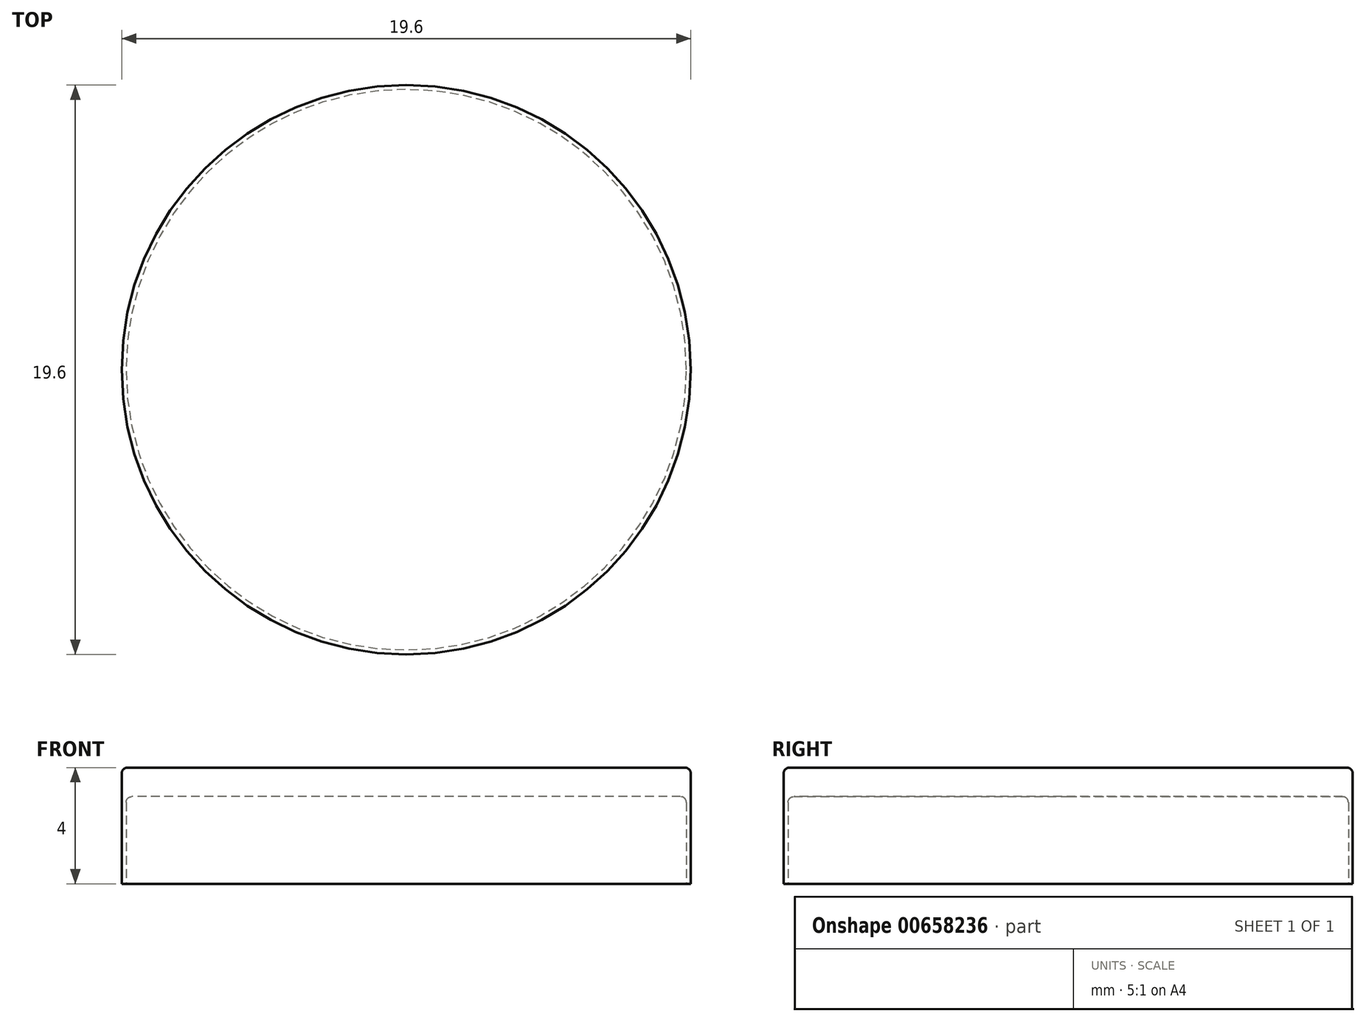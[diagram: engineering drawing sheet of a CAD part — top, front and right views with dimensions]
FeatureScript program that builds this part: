
annotation { "Feature Type Name" : "Feature", "Feature Type Description" : "" }
export const myFeature = defineFeature(function(context is Context, id is Id, definition is map)
    precondition{}
    {
        {
            var Q0;
            Q0=qCreatedBy(makeId("Top.planeOp"),FACE);
            var sketch = newSketch(context, id + "F0", { "sketchPlane" : qUnion([Q0])});
            skLineSegment(sketch, "E0", {"start": v(0, 0) * mm, "end": v(0, 0) * mm});
            skCircle(sketch, "E1", {"center": v(0, 0) * mm, "radius": 9.8 * mm});
            skCircle(sketch, "E2", {"center": v(0, 0) * mm, "radius": 9.65 * mm});
            skSolve(sketch);
        }
        {
            var Q0;
            Q0=makeQuery(id+"F0.imprint","IMPRINT",FACE,{"disambiguationData":[TD([[makeQuery(id+"F0.imprint","IMPRINT",EDGE,{"derivedFrom":sQuery(id+"F0.wireOp",EDGE,"E2")}),1.0]])]});
            var Q1;
            Q1=makeQuery(id+"F0.imprint","IMPRINT",FACE,{"disambiguationData":[TD([[makeQuery(id+"F0.imprint","IMPRINT",EDGE,{"derivedFrom":sQuery(id+"F0.wireOp",EDGE,"E1")}),1.0]])]});
            extrude(context, id + "F1", {"entities" : qUnion([Q0, Q1]), "depth" : 4 * mm, "offsetDistance" : 25 * mm});
        }
        {
            var Q0;
            Q0=makeQuery(id+"F0.imprint","IMPRINT",FACE,{"disambiguationData":[TD([[makeQuery(id+"F0.imprint","IMPRINT",EDGE,{"derivedFrom":sQuery(id+"F0.wireOp",EDGE,"E2")}),1.0]])]});
            extrude(context, id + "F2", {"entities" : qUnion([Q0]), "operationType" : NewBodyOperationType.REMOVE, "depth" : 3 * mm, "offsetDistance" : 25 * mm});
        }
        {
            var Q0;
            Q0=makeQuery(id+"F1.opExtrude","CAP_EDGE",EDGE,{"disambiguationData":[OSD([sQuery(id+"F0.wireOp",EDGE,"E1")])],"isStart":false});
            var Q1;
            Q1=makeQuery(id+"FNM5yF3ziWqO6u8_1.opExtrude","CAP_EDGE",EDGE,{"disambiguationData":[OSD([sQuery(id+"F0.wireOp",EDGE,"1752dfc6-2374-44e5-a3a8-89c9d2f55178")])],"isStart":false});
            var Q2;
            Q2=makeQuery(id+"F2.boolean.opBoolean","COPY",EDGE,{"derivedFrom":makeQuery(id+"F2.opExtrude","CAP_EDGE",EDGE,{"disambiguationData":[OSD([sQuery(id+"F0.wireOp",EDGE,"E2")])],"isStart":false})});
            var Q3;
            Q3=makeQuery(id+"FNM5yF3ziWqO6u8_1.opExtrude","CAP_EDGE",EDGE,{"disambiguationData":[OSD([sQuery(id+"F0.wireOp",EDGE,"1752dfc6-2374-44e5-a3a8-89c9d2f55178")])],"isStart":true});
            fillet(context, id + "F3", {"entities" : qUnion([Q0, Q1, Q2, Q3]), "radius" : 0.2 * mm, "tangentPropagation" : true, "allowEdgeOverflow" : false});
        }
    });
